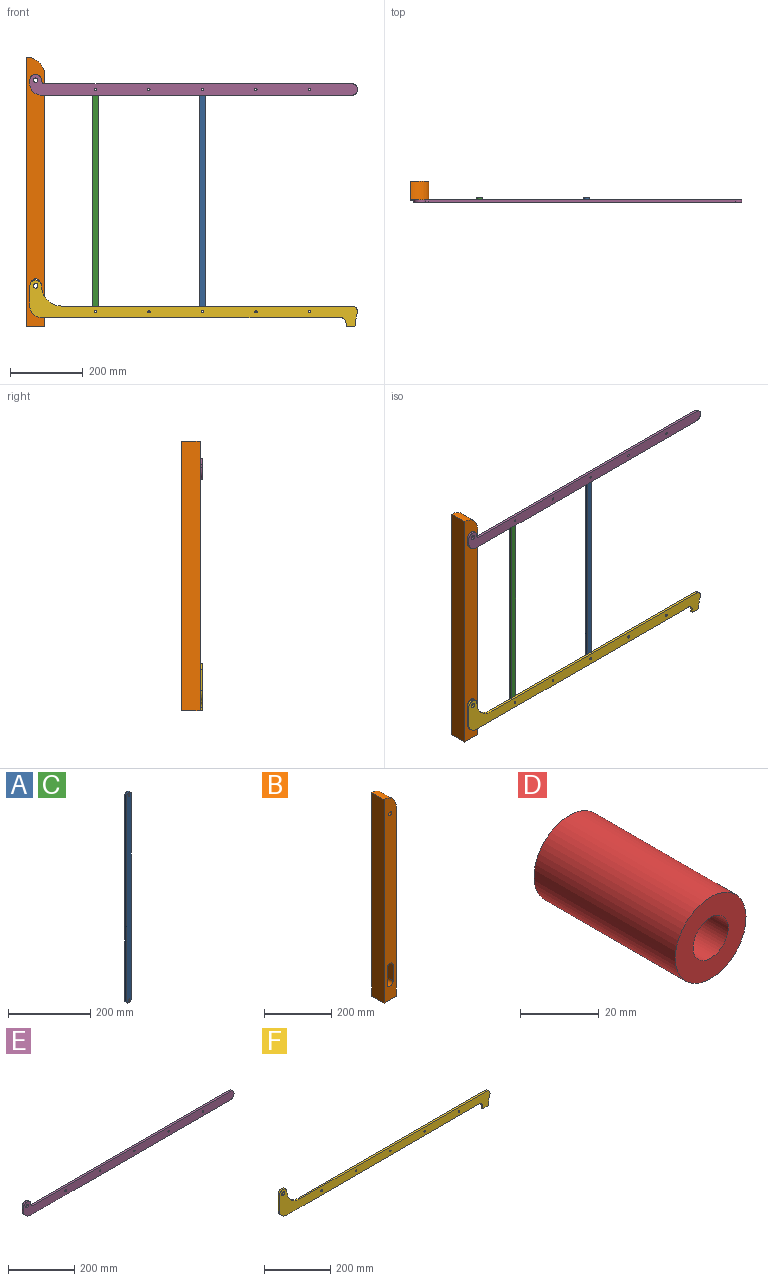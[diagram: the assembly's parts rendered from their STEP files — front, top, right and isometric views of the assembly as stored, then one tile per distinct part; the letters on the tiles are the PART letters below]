
ASSEMBLY  parts=6 mates=9
PART A: 8 faces, bbox 15.9x6.4x625.5 mm
  f0: plane 609.6x6.35mm, normal (1,0,0), area 3871mm2, adj f1,f4,f6,f7
  f1: cylinder r=7.94mm len=15.88mm, axis (0,1,0), area 158.3mm2, adj f0,f2,f6,f7
  f2: plane 609.6x6.35mm, normal (-1,0,0), area 3871mm2, adj f1,f4,f6,f7
  f3: cylinder r=3.17mm len=6.35mm, axis (0,1,0), area 126.7mm2, adj f6,f7
  f4: cylinder r=7.94mm len=15.88mm, axis (0,1,0), area 158.3mm2, adj f0,f2,f6,f7
  f5: cylinder r=3.17mm len=6.35mm, axis (0,1,0), area 126.7mm2, adj f6,f7
  f6: plane 625.48x15.88mm, normal (0,-1,0), area 9812mm2, adj f0,f1,f2,f3,f4,f5
  f7: plane 625.48x15.88mm, normal (0,1,0), area 9812mm2, adj f0,f1,f2,f3,f4,f5
PART B: 11 faces, bbox 50.8x50.8x739.6 mm
  f0: plane 739.56x50.8mm, normal (-1,0,0), area 37569.6mm2, adj f1,f8,f9,f10
  f1: plane 50.8x50.8mm, normal (0,0,-1), area 2580.6mm2, adj f0,f2,f9,f10
  f2: plane 688.76x50.8mm, normal (1,0,0), area 34989mm2, adj f1,f8,f9,f10
  f3: plane 57.16x50.8mm, normal (-1,0,0), area 2903.8mm2, adj f4,f6,f9,f10
  f4: cylinder r=12.7mm len=50.8mm, axis (0,1,0), area 2026.8mm2, adj f3,f5,f9,f10
  f5: plane 57.16x50.8mm, normal (1,0,0), area 2903.8mm2, adj f4,f6,f9,f10
  f6: cylinder r=12.7mm len=50.8mm, axis (0,1,0), area 2026.8mm2, adj f3,f5,f9,f10
  f7: cylinder r=6.35mm len=50.8mm, axis (0,1,0), area 2026.8mm2, adj f9,f10
  f8: cylinder r=50.8mm len=50.8mm, axis (0,1,0), area 4053.7mm2, adj f0,f2,f9,f10
  f9: plane 739.56x50.8mm, normal (0,-1,0), area 34930.5mm2, adj f0,f1,f2,f3,f4,f5,f6,f7
  f10: plane 739.56x50.8mm, normal (0,1,0), area 34930.5mm2, adj f0,f1,f2,f3,f4,f5,f6,f7
PART C: same geometry as A
PART D: 4 faces, bbox 25.4x50.8x25.4 mm
  f0: cylinder r=12.7mm len=50.8mm, axis (0,1,0), area 4053.7mm2, adj f2,f3
  f1: cylinder r=6.35mm len=50.8mm, axis (0,1,0), area 2026.8mm2, adj f2,f3
  f2: plane 25.4x25.4mm, normal (0,-1,0), area 380mm2, adj f0,f1
  f3: plane 25.4x25.4mm, normal (0,1,0), area 380mm2, adj f0,f1
PART E: 15 faces, bbox 898.5x6.4x56.9 mm
  f0: plane 9.31x6.35mm, normal (-1,0,0), area 59.1mm2, adj f1,f12,f13,f14
  f1: cylinder r=31.75mm len=31.75mm, axis (0,1,0), area 316.7mm2, adj f0,f2,f13,f14
  f2: plane 850.9x6.35mm, normal (0,0,-1), area 5403.2mm2, adj f1,f3,f13,f14
  f3: cylinder r=15.88mm len=31.75mm, axis (0,1,0), area 316.7mm2, adj f2,f4,f13,f14
  f4: plane 841.59x6.35mm, normal (0,0,1), area 5344.1mm2, adj f3,f5,f13,f14
  f5: cylinder r=9.31mm len=9.31mm, axis (0,1,0), area 92.9mm2, adj f4,f12,f13,f14
  f6: cylinder r=3.17mm len=6.35mm, axis (0,1,0), area 126.7mm2, adj f13,f14
  f7: cylinder r=6.35mm len=12.7mm, axis (0,1,0), area 253.4mm2, adj f13,f14
  f8: cylinder r=3.17mm len=6.35mm, axis (0,1,0), area 126.7mm2, adj f13,f14
  f9: cylinder r=3.17mm len=6.35mm, axis (0,1,0), area 126.7mm2, adj f13,f14
  f10: cylinder r=3.17mm len=6.35mm, axis (0,1,0), area 126.7mm2, adj f13,f14
  f11: cylinder r=3.17mm len=6.35mm, axis (0,1,0), area 126.7mm2, adj f13,f14
  f12: cylinder r=15.88mm len=31.75mm, axis (0,1,0), area 316.7mm2, adj f0,f5,f13,f14
  f13: plane 898.53x56.93mm, normal (0,-1,0), area 28628.7mm2, adj f0,f1,f2,f3,f4,f5,f6,f7
  f14: plane 898.53x56.93mm, normal (0,1,0), area 28628.7mm2, adj f0,f1,f2,f3,f4,f5,f6,f7
PART F: 19 faces, bbox 898.5x6.4x128.5 mm
  f0: plane 55.52x6.35mm, normal (-1,0,0), area 352.6mm2, adj f1,f15,f17,f18
  f1: cylinder r=31.75mm len=31.75mm, axis (0,1,0), area 316.7mm2, adj f0,f2,f17,f18
  f2: plane 819.15x6.35mm, normal (0,0,-1), area 5201.6mm2, adj f1,f3,f17,f18
  f3: cylinder r=15.88mm len=15.88mm, axis (0,1,0), area 158.3mm2, adj f2,f4,f17,f18
  f4: plane 9.53x6.35mm, normal (-1,0,0), area 60.5mm2, adj f3,f5,f17,f18
  f5: plane 24.53x6.35mm, normal (0,0,-1), area 155.8mm2, adj f4,f6,f17,f18
  f6: cylinder r=105.69mm len=35.89mm, axis (0,1,0), area 232.5mm2, adj f5,f7,f17,f18
  f7: cylinder r=15.88mm len=21.27mm, axis (0,1,0), area 193.3mm2, adj f6,f8,f17,f18
  f8: plane 795.38x6.35mm, normal (0,0,1), area 5050.6mm2, adj f7,f9,f17,f18
  f9: cylinder r=55.52mm len=55.52mm, axis (0,1,0), area 553.8mm2, adj f8,f15,f17,f18
  f10: cylinder r=3.17mm len=6.35mm, axis (0,1,0), area 126.7mm2, adj f17,f18
  f11: cylinder r=3.17mm len=6.35mm, axis (0,1,0), area 126.7mm2, adj f17,f18
  f12: cylinder r=3.17mm len=6.35mm, axis (0,1,0), area 126.7mm2, adj f17,f18
  f13: cylinder r=6.35mm len=12.7mm, axis (0,1,0), area 253.4mm2, adj f17,f18
  f14: cylinder r=3.17mm len=6.35mm, axis (0,1,0), area 126.7mm2, adj f17,f18
  f15: cylinder r=15.88mm len=31.75mm, axis (0,1,0), area 316.7mm2, adj f0,f9,f17,f18
  f16: cylinder r=3.17mm len=6.35mm, axis (0,1,0), area 126.7mm2, adj f17,f18
  f17: plane 898.53x128.55mm, normal (0,-1,0), area 31467mm2, adj f0,f1,f2,f3,f4,f5,f6,f7
  f18: plane 898.53x128.55mm, normal (0,1,0), area 31467mm2, adj f0,f1,f2,f3,f4,f5,f6,f7
PLACE A rot(axis=(0,-1,0),0deg) t=(293.16,-44.45,0)mm
PLACE B at identity
PLACE C rot(axis=(0,-1,0),0deg) t=(0,-44.45,0)mm
PLACE D rot(axis=(0,-1,0),90deg) t=(-563.38,0,-563.38)mm
PLACE E rot(axis=(0,-1,0),0deg) t=(0,-50.8,0)mm
PLACE F rot(axis=(0,-1,0),0deg) t=(0,-50.8,0)mm
MATE planar E.f14 <-> B.f8  axis (0,1,0) through (15.88,-50.8,-41.06)mm
MATE cylindrical C.f1 <-> E.f6  axis (0,-1,0) through (164.04,-50.8,-25.18)mm
MATE cylindrical C.f4 <-> F.f14  axis (0,-1,0) through (164.04,-50.8,-634.78)mm
MATE cylindrical A.f1 <-> E.f9  axis (0,-1,0) through (457.2,-50.8,-25.18)mm
MATE cylindrical A.f4 <-> F.f10  axis (0,-1,0) through (457.2,-50.8,-634.78)mm
MATE cylindrical E.f7 <-> B.f7  axis (0,1,0) through (0,-50.8,0)mm
MATE pin_slot D.f0 <-> B.f4  axis (0,-1,0) through (0,-50.8,-563.38)mm
MATE cylindrical D.f0 <-> F.f13  axis (0,-1,0) through (0,-50.8,-563.38)mm
MATE planar B.f9 <-> F.f1  axis (0,-1,0) through (-12.7,-50.8,-614.2)mm
